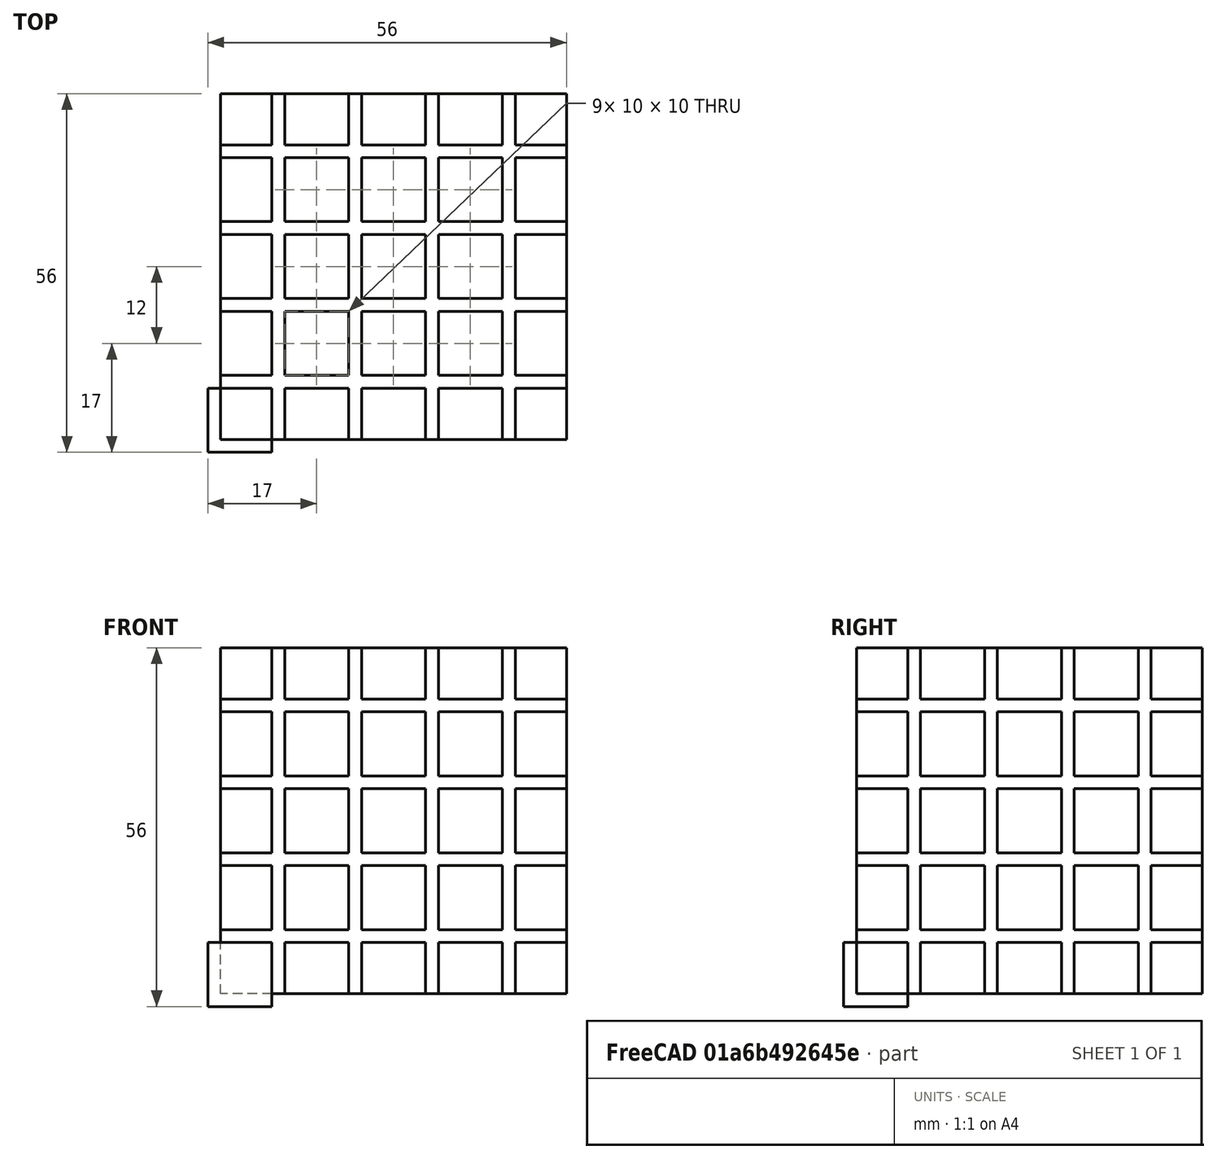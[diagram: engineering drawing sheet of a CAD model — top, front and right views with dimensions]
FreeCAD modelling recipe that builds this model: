
FCSTD DOCUMENT  (FreeCAD 1.0R39319 (Git))
Label: ojt1_t10p01_array
License: All rights reserved
LicenseURL: https://en.wikipedia.org/wiki/All_rights_reserved
objects: Part::Box×2, Part::FeaturePython×1, Part::Cut×1
note: 3 computed .brp shape members not serialized (recipe doc carries the construction recipe); baked Part::Feature solids carry a one-line shape summary decoded from their .brp

FEATURE [Part::Box] Box001  label="Cube"
  AttacherType = Attacher::AttachEngine3D
  Height = 54
  Length = 54
  Placement = pos=(2,2,2) rot=(0,0,1;0rad)
  Width = 54
FEATURE [Part::Box] Box  label="Cubo"
  AttacherType = Attacher::AttachEngine3D
  Height = 10
  Length = 10
  Width = 10
FEATURE [Part::FeaturePython] Array  # Draft array (typed FeaturePython)
  AlwaysSyncPlacement = false
  Angle = 360
  ArrayType = 0
  Axis = (0,0,1)
  Base = -> Box
  Center = (-23.34,11.94,0)
  Count = 125
  ExpandArray = false
  Fuse = false
  IntervalAxis = (0,0,0)
  IntervalX = (12,0,0)
  IntervalY = (0,12,0)
  IntervalZ = (0,0,12)
  NumberCircles = 3
  NumberPolar = 5
  NumberX = 5
  NumberY = 5
  NumberZ = 5
  PlacementList = 125 placements: [(0,0,0),(0,0,12),(0,0,24),(0,0,36),(0,0,48),(0,12,0),(0,12,12),(0,12,24),(0,12,36),(0,12,48),(0,24,0),(0,24,12),(0,24,24),(0,24,36),(0,24,48),(0,36,0),(0,36,12),(0,36,24),(0,36,36),(0,36,48),(0,48,0),(0,48,12),(0,48,24),(0,48,36),(0,48,48),(12,0,0),(12,0,12),(12,0,24),(12,0,36),(12,0,48),(12,12,0),(12,12,12),(12,12,24),(12,12,36),(12,12,48),(12,24,0),(12,24,12),(12,24,24),(12,24,36),(12,24,48),+85 more]
  RadialDistance = 50
  Symmetry = 1
  TangentialDistance = 25
FEATURE [Part::Cut] Cut
  Base = -> Box001
  Refine = true
  Tool = -> Array
